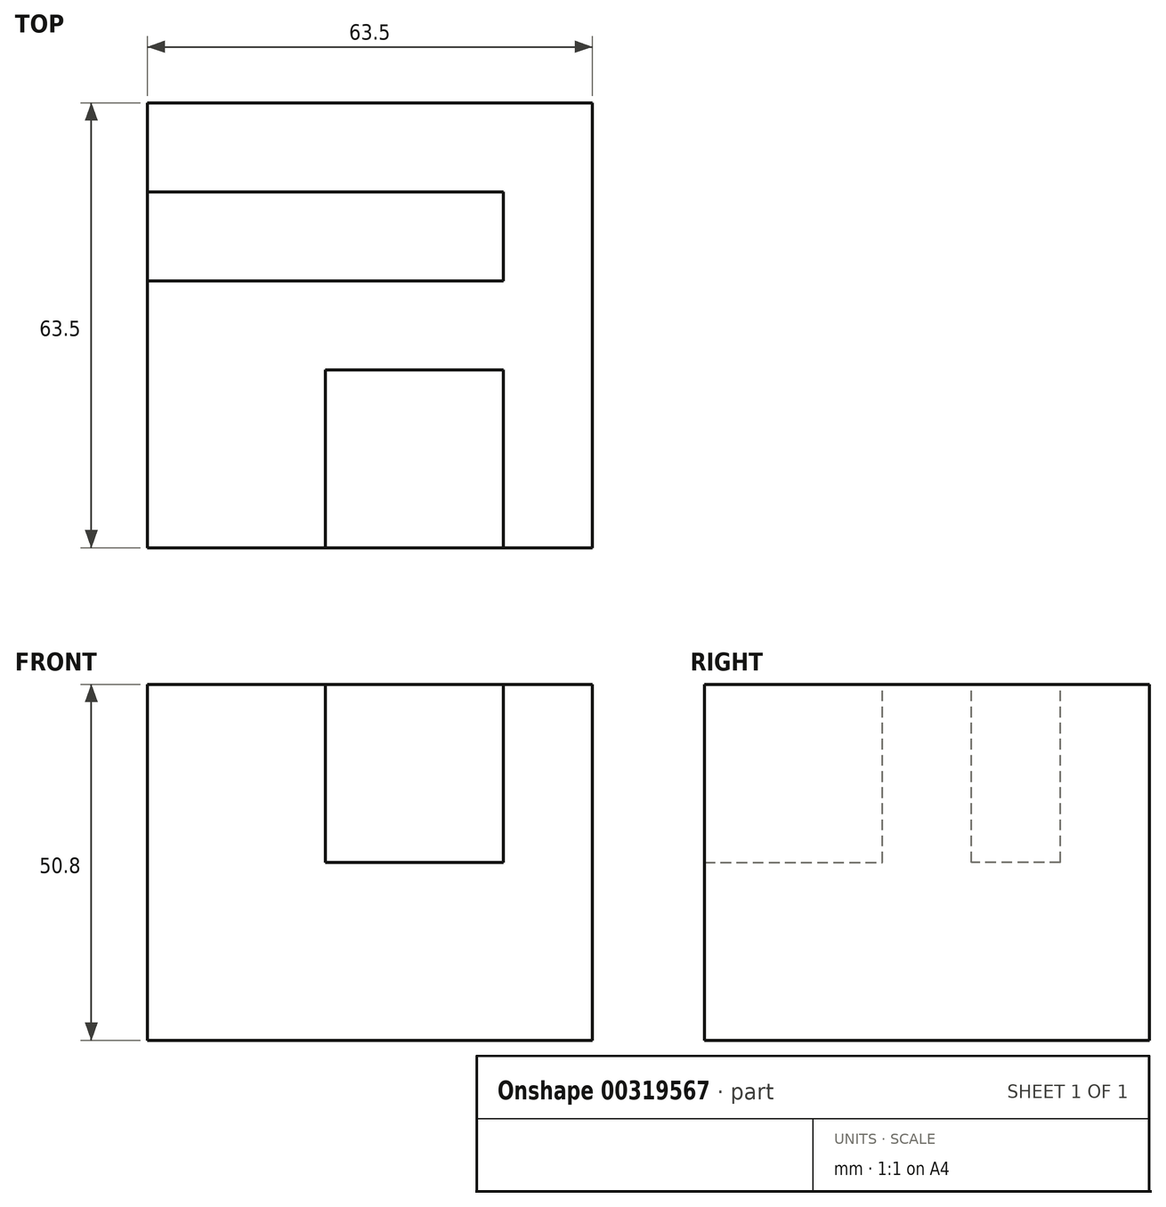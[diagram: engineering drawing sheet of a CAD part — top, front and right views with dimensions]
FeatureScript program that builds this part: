
annotation { "Feature Type Name" : "Feature", "Feature Type Description" : "" }
export const myFeature = defineFeature(function(context is Context, id is Id, definition is map)
    precondition{}
    {
        {
            var Q0;
            Q0=qCreatedBy(makeId("Top.planeOp"),FACE);
            var sketch = newSketch(context, id + "F0", { "sketchPlane" : qUnion([Q0])});
            skLineSegment(sketch, "E0", {"start": v(-30.8, -46.06) * mm, "end": v(32.7, -46.06) * mm});
            skLineSegment(sketch, "E1", {"start": v(32.7, -46.06) * mm, "end": v(32.7, 17.44) * mm});
            skLineSegment(sketch, "E2", {"start": v(32.7, 17.44) * mm, "end": v(-30.8, 17.44) * mm});
            skLineSegment(sketch, "E3", {"start": v(-30.8, 17.44) * mm, "end": v(-30.8, -46.06) * mm});
            skSolve(sketch);
        }
        {
            var Q0;
            Q0=makeQuery(id+"F0.imprint","IMPRINT",FACE,{"disambiguationData":[TD([[makeQuery(id+"F0.imprint","IMPRINT",EDGE,{"derivedFrom":sQuery(id+"F0.wireOp",EDGE,"E0")}),1.0]])]});
            extrude(context, id + "F1", {"entities" : qUnion([Q0]), "depth" : 50.8 * mm});
        }
        {
            var Q0;
            Q0=makeQuery(id+"F1.opExtrude","CAP_FACE",FACE,{"disambiguationData":[OSD([sQuery(id+"F0.wireOp",EDGE,"E0"),sQuery(id+"F0.wireOp",EDGE,"E1"),sQuery(id+"F0.wireOp",EDGE,"E2"),sQuery(id+"F0.wireOp",EDGE,"E3")])],"isStart":false});
            var sketch = newSketch(context, id + "F2", { "sketchPlane" : qUnion([Q0])});
            skLineSegment(sketch, "E4", {"start": v(32.7, -46.06) * mm, "end": v(20, -46.06) * mm});
            skLineSegment(sketch, "E5", {"start": v(20, -46.06) * mm, "end": v(20, -20.66) * mm});
            skLineSegment(sketch, "E6", {"start": v(20, -20.66) * mm, "end": v(-5.4, -20.66) * mm});
            skLineSegment(sketch, "E7", {"start": v(-5.4, -20.66) * mm, "end": v(-5.4, -46.06) * mm});
            skLineSegment(sketch, "E8", {"start": v(-5.4, -46.06) * mm, "end": v(20, -46.06) * mm});
            skSolve(sketch);
        }
        {
            var Q0;
            Q0=makeQuery(id+"F2.imprint","IMPRINT",FACE,{"disambiguationData":[TD([[makeQuery(id+"F2.imprint","IMPRINT",EDGE,{"derivedFrom":sQuery(id+"F2.wireOp",EDGE,"E5")}),1.0]])]});
            extrude(context, id + "F3", {"entities" : qUnion([Q0]), "operationType" : NewBodyOperationType.REMOVE, "oppositeDirection" : true, "depth" : 25.4 * mm});
        }
        {
            var Q0;
            Q0=makeQuery(id+"F1.opExtrude","CAP_FACE",FACE,{"disambiguationData":[OSD([sQuery(id+"F0.wireOp",EDGE,"E0"),sQuery(id+"F0.wireOp",EDGE,"E1"),sQuery(id+"F0.wireOp",EDGE,"E2"),sQuery(id+"F0.wireOp",EDGE,"E3")])],"isStart":false});
            var sketch = newSketch(context, id + "F4", { "sketchPlane" : qUnion([Q0])});
            skLineSegment(sketch, "E9", {"start": v(-30.8, 17.44) * mm, "end": v(-30.8, 4.74) * mm});
            skLineSegment(sketch, "E10", {"start": v(-30.8, 4.74) * mm, "end": v(20, 4.74) * mm});
            skLineSegment(sketch, "E11", {"start": v(20, 4.74) * mm, "end": v(20, -7.96) * mm});
            skLineSegment(sketch, "E12", {"start": v(20, -7.96) * mm, "end": v(-30.8, -7.96) * mm});
            skLineSegment(sketch, "E13", {"start": v(-30.8, -7.96) * mm, "end": v(-30.8, 4.74) * mm});
            skSolve(sketch);
        }
        {
            var Q0;
            Q0=makeQuery(id+"F4.imprint","IMPRINT",FACE,{"disambiguationData":[TD([[makeQuery(id+"F4.imprint","IMPRINT",EDGE,{"derivedFrom":sQuery(id+"F4.wireOp",EDGE,"E10")}),-1.0]])]});
            extrude(context, id + "F5", {"entities" : qUnion([Q0]), "operationType" : NewBodyOperationType.REMOVE, "oppositeDirection" : true, "depth" : 25.4 * mm});
        }
    });
